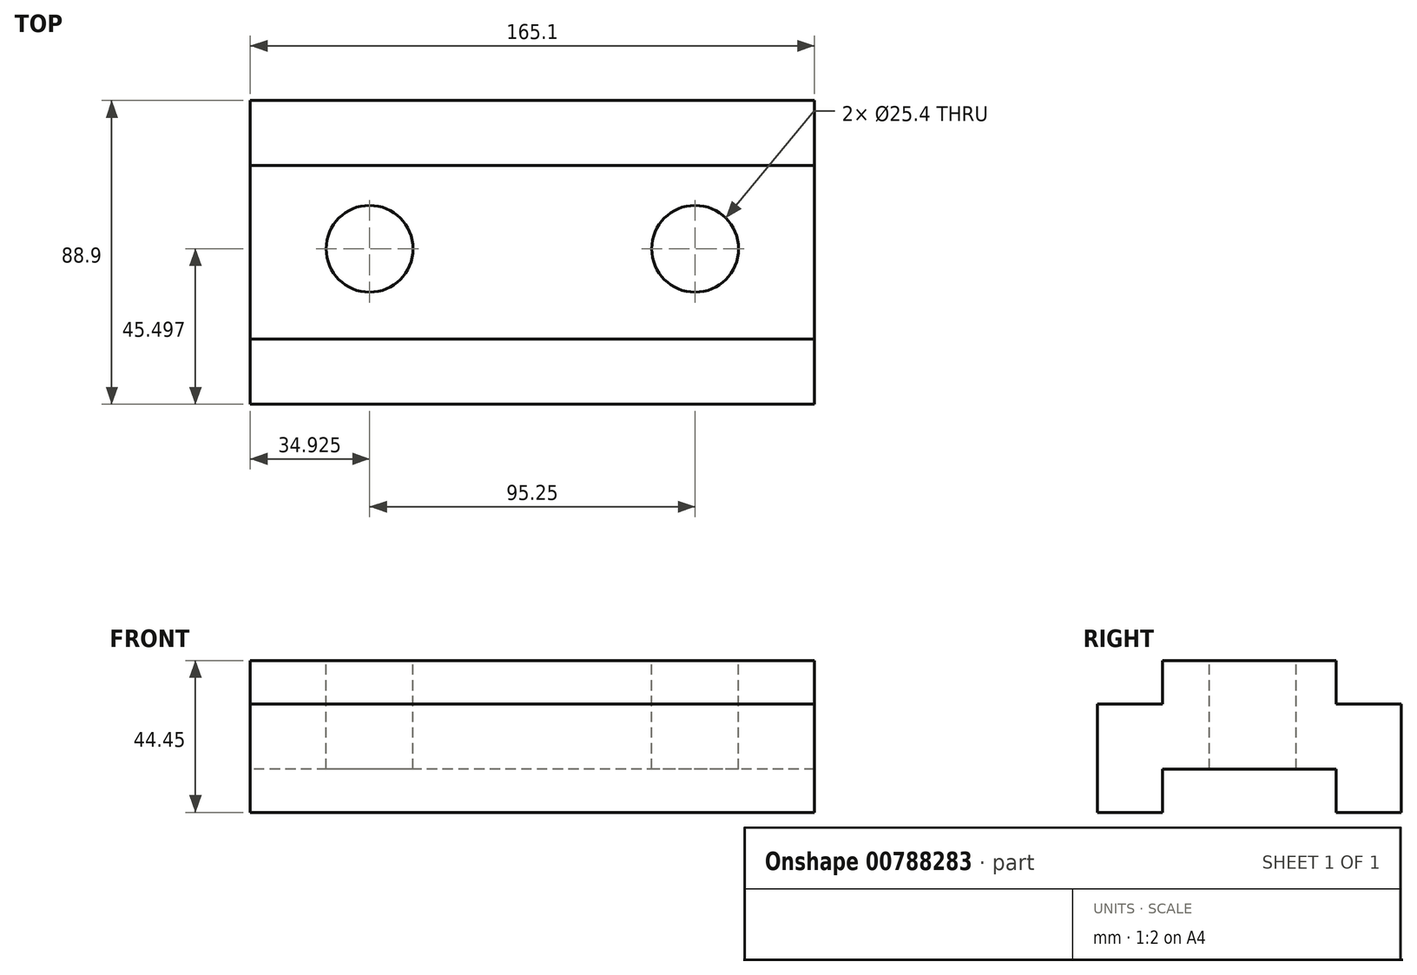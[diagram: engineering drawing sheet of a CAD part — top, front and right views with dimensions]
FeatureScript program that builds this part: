
annotation { "Feature Type Name" : "Feature", "Feature Type Description" : "" }
export const myFeature = defineFeature(function(context is Context, id is Id, definition is map)
    precondition{}
    {
        {
            var Q0;
            Q0=qCreatedBy(makeId("Right.planeOp"),FACE);
            var sketch = newSketch(context, id + "F0", { "sketchPlane" : qUnion([Q0])});
            skLineSegment(sketch, "E0", {"start": v(0, 0) * mm, "end": v(19.05, 0) * mm});
            skLineSegment(sketch, "E1", {"start": v(19.05, 0) * mm, "end": v(19.05, 12.7) * mm});
            skLineSegment(sketch, "E2", {"start": v(19.05, 12.7) * mm, "end": v(69.85, 12.7) * mm});
            skLineSegment(sketch, "E3", {"start": v(69.85, 12.7) * mm, "end": v(69.85, 0) * mm});
            skLineSegment(sketch, "E4", {"start": v(69.85, 0) * mm, "end": v(88.9, 0) * mm});
            skLineSegment(sketch, "E5", {"start": v(88.9, 0) * mm, "end": v(88.9, 31.75) * mm});
            skLineSegment(sketch, "E6", {"start": v(88.9, 31.75) * mm, "end": v(69.85, 31.75) * mm});
            skLineSegment(sketch, "E7", {"start": v(0, 0) * mm, "end": v(0, 31.75) * mm});
            skLineSegment(sketch, "E8", {"start": v(0, 31.75) * mm, "end": v(19.05, 31.75) * mm});
            skLineSegment(sketch, "E9", {"start": v(19.05, 31.75) * mm, "end": v(19.05, 44.45) * mm});
            skLineSegment(sketch, "E10", {"start": v(19.05, 44.45) * mm, "end": v(69.85, 44.45) * mm});
            skLineSegment(sketch, "E11", {"start": v(69.85, 44.45) * mm, "end": v(69.85, 31.75) * mm});
            skSolve(sketch);
        }
        {
            var Q0;
            Q0=makeQuery(id+"F0.imprint","IMPRINT",FACE,{"disambiguationData":[TD([[makeQuery(id+"F0.imprint","IMPRINT",EDGE,{"derivedFrom":sQuery(id+"F0.wireOp",EDGE,"E0")}),1.0]])]});
            extrude(context, id + "F1", {"entities" : qUnion([Q0]), "depth" : 165.1 * mm, "offsetDistance" : 25.4 * mm});
        }
        {
            var Q0;
            Q0=makeQuery(id+"F1.opExtrude","SWEPT_FACE",FACE,{"disambiguationData":[OSD([sQuery(id+"F0.wireOp",EDGE,"E10")])]});
            var sketch = newSketch(context, id + "F2", { "sketchPlane" : qUnion([Q0])});
            skSolve(sketch);
        }
        {
            var Q0;
            {var subQ0=sQuery(id+"F0.wireOp",EDGE,"E10");Q0=makeQuery(id+"F2.imprint","IMPRINT",FACE,{"disambiguationData":[TD([[makeQuery(id+"F2.imprint","IMPRINT",EDGE,{"derivedFrom":makeQuery(id+"F1.opExtrude","CAP_EDGE",EDGE,{"disambiguationData":[OSD([subQ0])],"isStart":true})}),-1.0]])]});}
            var sketch = newSketch(context, id + "F3", { "sketchPlane" : qUnion([Q0])});
            skLineSegment(sketch, "E12", {"start": v(0, 45.5) * mm, "end": v(34.93, 45.5) * mm, "construction": true});
            skLineSegment(sketch, "E13", {"start": v(34.93, 45.5) * mm, "end": v(130.18, 45.5) * mm, "construction": true});
            skCircle(sketch, "E14", {"center": v(34.93, 45.5) * mm, "radius": 12.7 * mm});
            skCircle(sketch, "E15", {"center": v(130.18, 45.5) * mm, "radius": 12.7 * mm});
            skSolve(sketch);
        }
        {
            var Q0;
            Q0=makeQuery(id+"F3.imprint","IMPRINT",FACE,{"disambiguationData":[TD([[makeQuery(id+"F3.imprint","IMPRINT",EDGE,{"derivedFrom":sQuery(id+"F3.wireOp",EDGE,"E14")}),1.0]])]});
            var Q1;
            Q1=makeQuery(id+"F3.imprint","IMPRINT",FACE,{"disambiguationData":[TD([[makeQuery(id+"F3.imprint","IMPRINT",EDGE,{"derivedFrom":sQuery(id+"F3.wireOp",EDGE,"E15")}),1.0]])]});
            extrude(context, id + "F4", {"entities" : qUnion([Q0, Q1]), "operationType" : NewBodyOperationType.REMOVE, "endBound" : BoundingType.UP_TO_NEXT, "oppositeDirection" : true, "depth" : 25.4 * mm, "offsetDistance" : 25.4 * mm});
        }
    });
